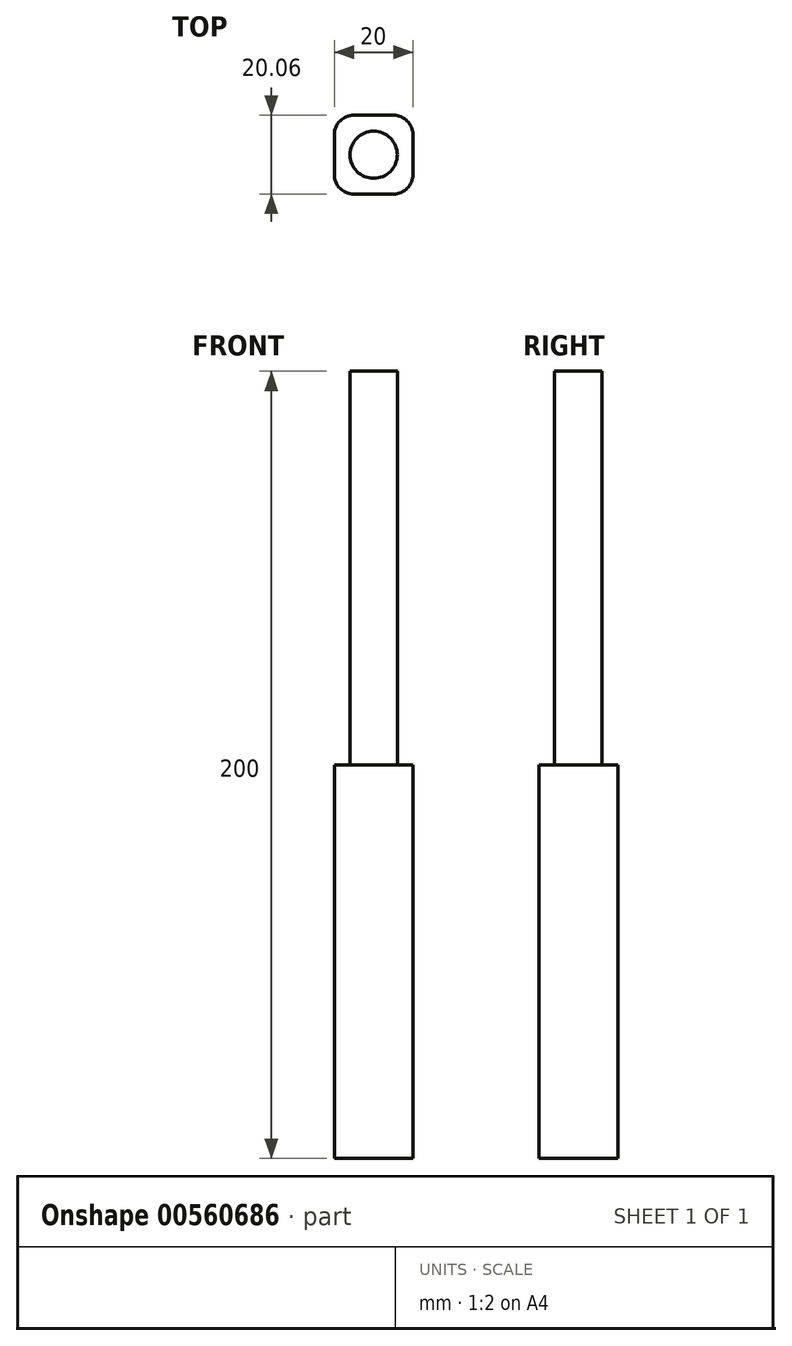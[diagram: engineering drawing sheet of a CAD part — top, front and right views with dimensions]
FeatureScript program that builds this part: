
annotation { "Feature Type Name" : "Feature", "Feature Type Description" : "" }
export const myFeature = defineFeature(function(context is Context, id is Id, definition is map)
    precondition{}
    {
        {
            var Q0;
            Q0=qCreatedBy(makeId("Top.planeOp"),FACE);
            var sketch = newSketch(context, id + "F0", { "sketchPlane" : qUnion([Q0])});
            skCircle(sketch, "E0", {"center": v(0, 0) * mm, "radius": 6 * mm});
            skSolve(sketch);
        }
        {
            var Q0;
            Q0 = qSketchRegion(id + "F0", true);
            extrude(context, id + "F1", {"entities" : qUnion([Q0]), "depth" : 100 * mm, "offsetDistance" : 25 * mm});
        }
        {
            var Q0;
            Q0=makeQuery(id+"F1.opExtrude","CAP_FACE",FACE,{"disambiguationData":[OSD([sQuery(id+"F0.wireOp",EDGE,"E0")])],"isStart":true});
            var sketch = newSketch(context, id + "F2", { "sketchPlane" : qUnion([Q0])});
            skLineSegment(sketch, "E1", {"start": v(0, 6) * mm, "end": v(0, 10) * mm});
            skLineSegment(sketch, "E2", {"start": v(-6, 0) * mm, "end": v(-10, 0) * mm});
            skLineSegment(sketch, "E3", {"start": v(6, 0) * mm, "end": v(10, 0) * mm});
            skLineSegment(sketch, "E4", {"start": v(0, -6) * mm, "end": v(0, -10) * mm});
            skLineSegment(sketch, "E5.bottom", {"start": v(5, 10) * mm, "end": v(-5, 10) * mm});
            skLineSegment(sketch, "E5.top", {"start": v(5, -10.06) * mm, "end": v(-5, -10.06) * mm});
            skLineSegment(sketch, "E5.left", {"start": v(10, 5) * mm, "end": v(10, -5.06) * mm});
            skLineSegment(sketch, "E5.right", {"start": v(-10, 5) * mm, "end": v(-10, -5.06) * mm});
            skPoint(sketch, "E6.visualSharp", {"position": v(-10, 10) * mm});
            skArc(sketch, "E6.filletArc", {"start": v(-5, 10) * mm, "mid": v(-8.54, 8.54) * mm, "end": v(-10, 5) * mm});
            skPoint(sketch, "E7.visualSharp", {"position": v(10, 10) * mm});
            skArc(sketch, "E7.filletArc", {"start": v(10, 5) * mm, "mid": v(8.54, 8.54) * mm, "end": v(5, 10) * mm});
            skPoint(sketch, "E8.visualSharp", {"position": v(10, -10.06) * mm});
            skArc(sketch, "E8.filletArc", {"start": v(5, -10.06) * mm, "mid": v(8.54, -8.6) * mm, "end": v(10, -5.06) * mm});
            skPoint(sketch, "E9.visualSharp", {"position": v(-10, -10.06) * mm});
            skArc(sketch, "E9.filletArc", {"start": v(-10, -5.06) * mm, "mid": v(-8.54, -8.6) * mm, "end": v(-5, -10.06) * mm});
            skSolve(sketch);
        }
        {
            var Q0;
            Q0 = qSketchRegion(id + "F2", true);
            extrude(context, id + "F3", {"entities" : qUnion([Q0]), "operationType" : NewBodyOperationType.ADD, "depth" : 100 * mm, "offsetDistance" : 25 * mm});
        }
    });
